# Revit family: precast panel
name_source: partatom
category: Curtain Panels
revit_build: Autodesk Revit Architecture 2013 (Build: 20120221_2030)
units: mm (PartAtom-declared; Revit-internal decimal feet)

## types (5) — shared parameters
Analytic Construction = <None>
END JOINT = No
FRAME_INSET = 0' - 1"
FRAME_WIDTH = 0' - 1"
GLASS_INSET = 0' - 1"
GLASS_THICKNESS = 0' - 1"
JT_HALF = 0' - 0 1/2"
JT_LEFT = 0' - 0 1/2"
JT_RIGHT = 0' - 0 1/2"
JT_TOP = 0' - 0 1/2"
JT_TYP = 0' - 1"
LEFT = No
PANEL_DEPTH = 0' - 6"
RIGHT = No
TOP = No
VOID_WALL INPUT = 2' - 0"
WIN2 = Yes
WIN2_PANEL VOID = 0' - 6"
WIN2_WALL VOID = 2' - 0"
WIN3_LEFT = 2' - 10"

## per-type parameters (varying)
| type | WIN1 | WIN1_PANEL VOID | WIN1_RIGHT | WIN1_WALL VOID | WIN2_LEFT | WIN2_RIGHT | WIN3 | WIN3_PANEL VOID | WIN3_WALL VOID |
| 3 | Yes | 0' - 6" | 2' - 0" | 2' - 0" | 3' - 6" | 5' - 0" | Yes | 0' - 6" | 2' - 0" |
| 1 | Yes | 0' - 6" | 1' - 6" | 2' - 0" | 3' - 0" | 2' - 0" | No | -0' - 0 1/8" | 0' - 0" |
| 2 | Yes | 0' - 6" | 2' - 10" | 2' - 0" | 5' - 0" | 1' - 6" | No | -0' - 0 1/8" | 0' - 0" |
| 4 | No | -0' - 0 1/8" | 2' - 0" | 0' - 0" | 2' - 0" | 2' - 0" | No | -0' - 0 1/8" | 0' - 0" |
| 5 | No | -0' - 0 1/8" | 2' - 0" | 0' - 0" | 1' - 6" | 5' - 0" | Yes | 0' - 6" | 2' - 0" |

## geometry (parser evidence)
native form markers: Blend x16, Sweep x3
no freeform markers — native parametric forms only
